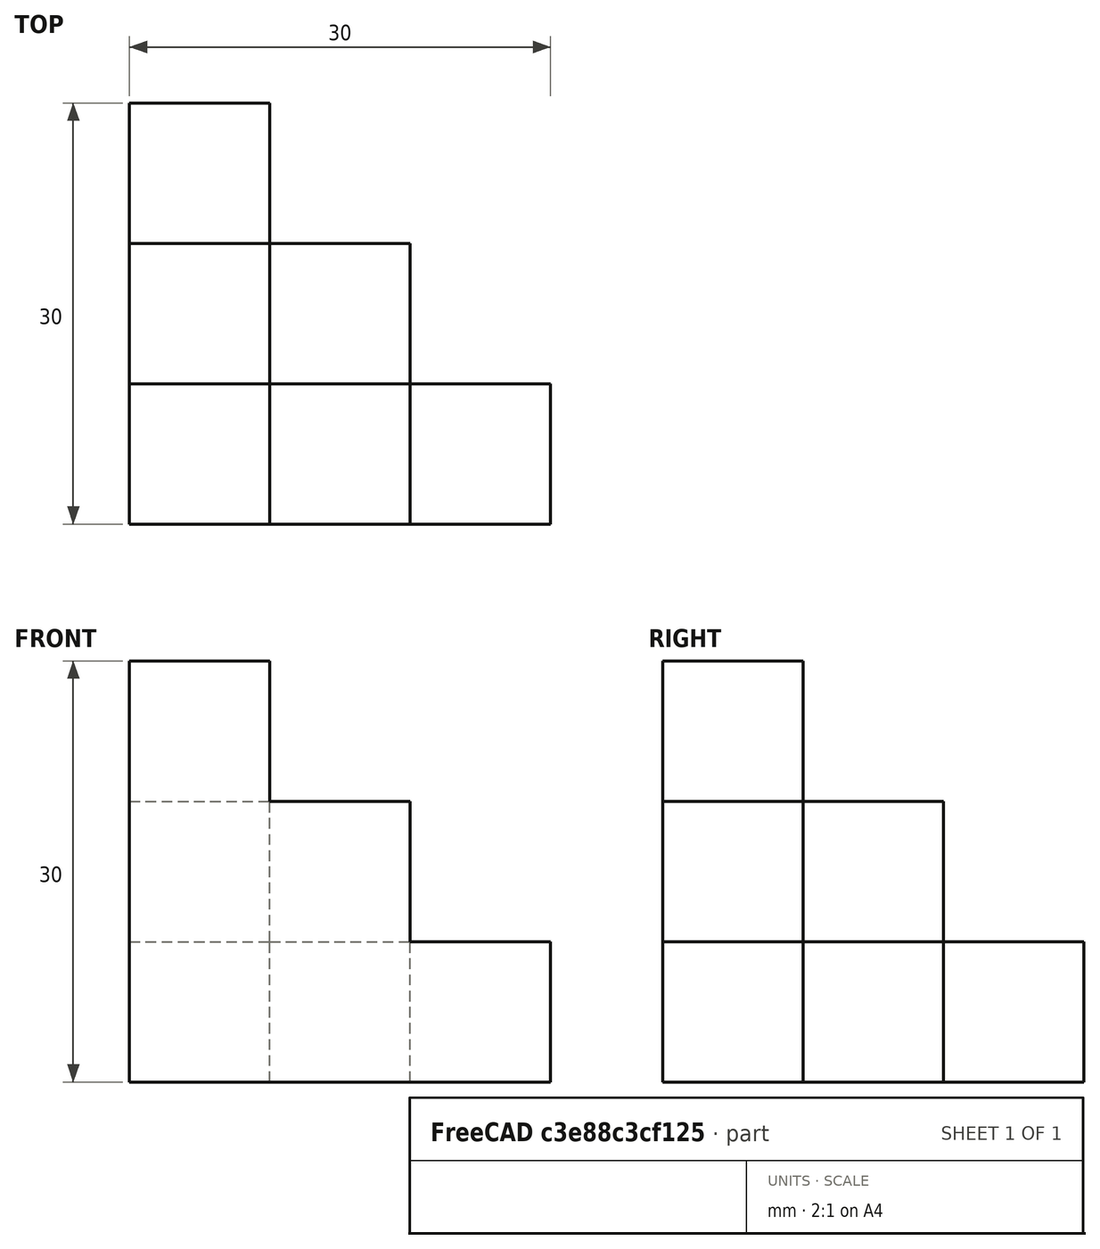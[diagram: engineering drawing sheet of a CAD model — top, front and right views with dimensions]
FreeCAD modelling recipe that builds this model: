
FCSTD DOCUMENT  (FreeCAD 1.0R39319 (Git))
Label: ojt1_t05r02_refineQbert_3-levels
License: All rights reserved
LicenseURL: https://en.wikipedia.org/wiki/All_rights_reserved
objects: Part::Box×10, Part::MultiFuse×1
note: 11 computed .brp shape members not serialized (recipe doc carries the construction recipe); baked Part::Feature solids carry a one-line shape summary decoded from their .brp

FEATURE [Part::Box] Box  label="Cub"
  AttacherType = Attacher::AttachEngine3D
  Height = 10
  Length = 10
  Width = 10
FEATURE [Part::Box] Box001  label="Cub001"
  AttacherType = Attacher::AttachEngine3D
  Height = 10
  Length = 10
  Placement = pos=(10,0,0) rot=(0,0,1;0rad)
  Width = 10
FEATURE [Part::Box] Box002  label="Cub002"
  AttacherType = Attacher::AttachEngine3D
  Height = 10
  Length = 10
  Placement = pos=(0,10,0) rot=(0,0,1;0rad)
  Width = 10
FEATURE [Part::Box] Box003  label="Cub003"
  AttacherType = Attacher::AttachEngine3D
  Height = 10
  Length = 10
  Placement = pos=(0,0,10) rot=(0,0,1;0rad)
  Width = 10
FEATURE [Part::Box] Box004  label="Cub004"
  AttacherType = Attacher::AttachEngine3D
  Height = 10
  Length = 10
  Placement = pos=(0,0,20) rot=(0,0,1;0rad)
  Width = 10
FEATURE [Part::Box] Box005  label="Cub005"
  AttacherType = Attacher::AttachEngine3D
  Height = 10
  Length = 10
  Placement = pos=(10,0,10) rot=(0,0,1;0rad)
  Width = 10
FEATURE [Part::Box] Box006  label="Cub006"
  AttacherType = Attacher::AttachEngine3D
  Height = 10
  Length = 10
  Placement = pos=(20,0,0) rot=(0,0,1;0rad)
  Width = 10
FEATURE [Part::Box] Box007  label="Cub007"
  AttacherType = Attacher::AttachEngine3D
  Height = 10
  Length = 10
  Placement = pos=(0,10,10) rot=(0,0,1;0rad)
  Width = 10
FEATURE [Part::Box] Box008  label="Cub008"
  AttacherType = Attacher::AttachEngine3D
  Height = 10
  Length = 10
  Placement = pos=(10,10,0) rot=(0,0,1;0rad)
  Width = 10
FEATURE [Part::Box] Box009  label="Cub009"
  AttacherType = Attacher::AttachEngine3D
  Height = 10
  Length = 10
  Placement = pos=(0,20,0) rot=(0,0,1;0rad)
  Width = 10
FEATURE [Part::MultiFuse] Fusion
  Refine = true
  Shapes = -> [Box,Box001,Box002,Box003,Box004,Box005,Box006,Box007,Box008,Box009]
